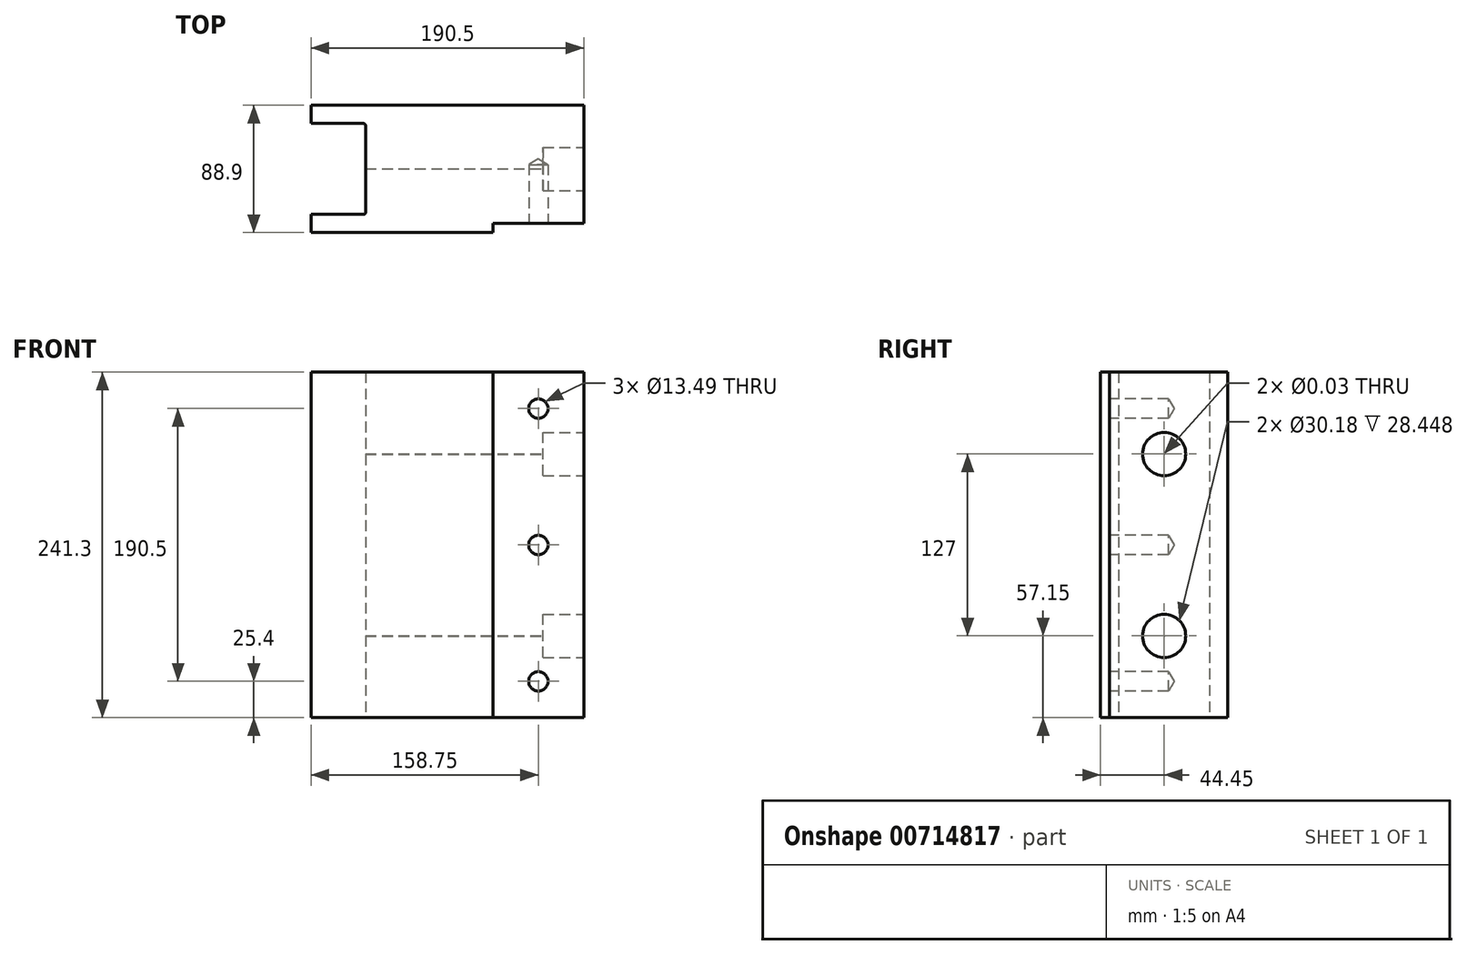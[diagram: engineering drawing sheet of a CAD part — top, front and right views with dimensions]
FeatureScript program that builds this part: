
annotation { "Feature Type Name" : "Feature", "Feature Type Description" : "" }
export const myFeature = defineFeature(function(context is Context, id is Id, definition is map)
    precondition{}
    {
        {
            var Q0;
            Q0=qCreatedBy(makeId("Top.planeOp"),FACE);
            var sketch = newSketch(context, id + "F0", { "sketchPlane" : qUnion([Q0])});
            skLineSegment(sketch, "E0.bottom", {"start": v(-95.25, 44.45) * mm, "end": v(95.25, 44.45) * mm});
            skLineSegment(sketch, "E0.top", {"start": v(-95.25, -44.45) * mm, "end": v(95.25, -44.45) * mm});
            skLineSegment(sketch, "E0.left", {"start": v(-95.25, 44.45) * mm, "end": v(-95.25, 31.75) * mm});
            skLineSegment(sketch, "E0.right", {"start": v(95.25, 44.45) * mm, "end": v(95.25, -44.45) * mm});
            skPoint(sketch, "E0.middle", {"position": v(0, 0) * mm});
            skLineSegment(sketch, "E1.bottom", {"start": v(-57.15, -31.75) * mm, "end": v(-133.35, -31.75) * mm});
            skLineSegment(sketch, "E1.top", {"start": v(-57.15, 31.75) * mm, "end": v(-133.35, 31.75) * mm});
            skLineSegment(sketch, "E1.left", {"start": v(-57.15, -31.75) * mm, "end": v(-57.15, 31.75) * mm});
            skPoint(sketch, "E1.middle", {"position": v(-95.25, 0) * mm});
            skLineSegment(sketch, "E2.trimOffspring", {"start": v(-95.25, 0) * mm, "end": v(-95.25, -44.45) * mm});
            skSolve(sketch);
        }
        {
            var Q0;
            Q0 = qSketchRegion(id + "F0", true);
            extrude(context, id + "F1", {"entities" : qUnion([Q0]), "endBound" : BoundingType.SYMMETRIC, "depth" : 241.3 * mm, "offsetDistance" : 25.4 * mm});
        }
        {
            var Q0;
            Q0=makeQuery(id+"F1.opExtrude","SWEPT_EDGE",EDGE,{"disambiguationData":[OSD([sQuery(id+"F0.wireOp",EDGE,"E1.top"),sQuery(id+"F0.wireOp",EDGE,"E1.left")])]});
            var Q1;
            Q1=makeQuery(id+"F1.opExtrude","SWEPT_EDGE",EDGE,{"disambiguationData":[OSD([sQuery(id+"F0.wireOp",EDGE,"E1.bottom"),sQuery(id+"F0.wireOp",EDGE,"E1.left")])]});
            fillet(context, id + "F2", {"entities" : qUnion([Q0, Q1]), "radius" : 1.52 * mm, "tangentPropagation" : true, "allowEdgeOverflow" : false});
        }
        {
            var Q0;
            Q0=makeQuery(id+"F1.opExtrude","SWEPT_FACE",FACE,{"disambiguationData":[OSD([sQuery(id+"F0.wireOp",EDGE,"E0.right")])]});
            var sketch = newSketch(context, id + "F3", { "sketchPlane" : qUnion([Q0])});
            skLineSegment(sketch, "E3", {"start": v(0, -145.44) * mm, "end": v(0, 141.68) * mm, "construction": true});
            skLineSegment(sketch, "E4.0", {"start": v(44.45, -120.65) * mm, "end": v(-44.45, -120.65) * mm, "construction": true});
            skLineSegment(sketch, "E5.0", {"start": v(44.45, -63.5) * mm, "end": v(-44.45, -63.5) * mm, "construction": true});
            skLineSegment(sketch, "E6.0", {"start": v(44.45, 63.5) * mm, "end": v(-44.45, 63.5) * mm, "construction": true});
            skPoint(sketch, "E7", {"position": v(0, 63.5) * mm});
            skPoint(sketch, "E8", {"position": v(0, -63.5) * mm});
            skSolve(sketch);
        }
        {
            var Q0;
            Q0=sQuery(id+"F3.wireOp",VERTEX,"E7");
            var Q1;
            Q1=sQuery(id+"F3.wireOp",VERTEX,"E8");
            var Q2;
            Q2=makeQuery(id+"F1.opExtrude","SWEPT_BODY",BODY,{"disambiguationData":[OSD([sQuery(id+"F0.wireOp",EDGE,"E0.bottom"),sQuery(id+"F0.wireOp",EDGE,"E0.top"),sQuery(id+"F0.wireOp",EDGE,"E0.left"),sQuery(id+"F0.wireOp",EDGE,"E0.right"),sQuery(id+"F0.wireOp",EDGE,"E1.bottom"),sQuery(id+"F0.wireOp",EDGE,"E1.top"),sQuery(id+"F0.wireOp",EDGE,"E1.left"),sQuery(id+"F0.wireOp",EDGE,"E2.trimOffspring")])]});
            hole(context, id + "F4", {"style" : HoleStyle.C_BORE, "endStyle" : HoleEndStyle.THROUGH, "standardTappedOrClearance" : lookupTablePath({ "standard" : "ANSI", "size" : "13/16 (0.81)", "type" : "Drilled" }), "standardBlindInLast" : lookupTablePath({ "standard" : "ANSI", "size" : "13/16", "type" : "Drilled" }), "holeDiameter" : 13 / 406.4 * mm, "cBoreDiameter" : 30.18 * mm, "cBoreDepth" : 28.45 * mm, "majorDiameter" : 6.35 * mm, "isTappedThrough" : true, "tappedDepth" : 34.3 * mm, "tapClearance" : 3, "locations" : qUnion([Q0, Q1]), "scope" : qUnion([Q2])});
        }
        {
            var Q0;
            Q0=makeQuery(id+"F1.opExtrude","SWEPT_FACE",FACE,{"disambiguationData":[OSD([sQuery(id+"F0.wireOp",EDGE,"E0.top")])]});
            var sketch = newSketch(context, id + "F5", { "sketchPlane" : qUnion([Q0])});
            skLineSegment(sketch, "E9.bottom", {"start": v(95.25, 120.65) * mm, "end": v(31.75, 120.65) * mm});
            skLineSegment(sketch, "E9.top", {"start": v(95.25, -120.65) * mm, "end": v(31.75, -120.65) * mm});
            skLineSegment(sketch, "E9.left", {"start": v(95.25, 120.65) * mm, "end": v(95.25, -120.65) * mm});
            skLineSegment(sketch, "E9.right", {"start": v(31.75, 120.65) * mm, "end": v(31.75, -120.65) * mm});
            skSolve(sketch);
        }
        {
            var Q0;
            Q0 = qSketchRegion(id + "F5", true);
            extrude(context, id + "F6", {"entities" : qUnion([Q0]), "operationType" : NewBodyOperationType.REMOVE, "oppositeDirection" : true, "depth" : 6.35 * mm, "offsetDistance" : 25.4 * mm});
        }
        {
            var Q0;
            Q0=makeQuery(id+"F6.boolean.opBoolean","COPY",FACE,{"derivedFrom":makeQuery(id+"F6.opExtrude","CAP_FACE",FACE,{"disambiguationData":[OSD([sQuery(id+"F5.wireOp",EDGE,"E9.bottom"),sQuery(id+"F5.wireOp",EDGE,"E9.top"),sQuery(id+"F5.wireOp",EDGE,"E9.left"),sQuery(id+"F5.wireOp",EDGE,"E9.right")])],"isStart":false})});
            var sketch = newSketch(context, id + "F7", { "sketchPlane" : qUnion([Q0])});
            skLineSegment(sketch, "E10.0", {"start": v(95.25, 120.65) * mm, "end": v(95.25, -120.65) * mm, "construction": true});
            skLineSegment(sketch, "E11", {"start": v(173.2, 0) * mm, "end": v(-136.03, 0) * mm, "construction": true});
            skLineSegment(sketch, "E12.0", {"start": v(63.5, 120.65) * mm, "end": v(63.5, -120.65) * mm, "construction": true});
            skLineSegment(sketch, "E13.0", {"start": v(173.2, 95.25) * mm, "end": v(-136.03, 95.25) * mm, "construction": true});
            skPoint(sketch, "E14", {"position": v(63.5, 95.25) * mm});
            skPoint(sketch, "E15", {"position": v(63.5, 0) * mm});
            skPoint(sketch, "E16.MirrorP", {"position": v(63.5, -95.25) * mm});
            skSolve(sketch);
        }
        {
            var Q0;
            Q0=sQuery(id+"F7.wireOp",VERTEX,"E14");
            var Q1;
            Q1=sQuery(id+"F7.wireOp",VERTEX,"E15");
            var Q2;
            Q2=sQuery(id+"F7.wireOp",VERTEX,"E16.MirrorP");
            var Q3;
            Q3=makeQuery(id+"F1.opExtrude","SWEPT_BODY",BODY,{"disambiguationData":[OSD([sQuery(id+"F0.wireOp",EDGE,"E0.bottom"),sQuery(id+"F0.wireOp",EDGE,"E0.top"),sQuery(id+"F0.wireOp",EDGE,"E0.left"),sQuery(id+"F0.wireOp",EDGE,"E0.right"),sQuery(id+"F0.wireOp",EDGE,"E1.bottom"),sQuery(id+"F0.wireOp",EDGE,"E1.top"),sQuery(id+"F0.wireOp",EDGE,"E1.left"),sQuery(id+"F0.wireOp",EDGE,"E2.trimOffspring")])]});
            hole(context, id + "F8", {"style" : HoleStyle.SIMPLE, "endStyle" : HoleEndStyle.BLIND, "standardTappedOrClearance" : lookupTablePath({ "standard" : "ANSI", "engagement" : "75%", "pitch" : "11 tpi", "size" : "5/8", "type" : "Tapped" }), "standardBlindInLast" : lookupTablePath({ "standard" : "ANSI", "engagement" : "75%", "pitch" : "11 tpi", "size" : "5/8", "type" : "Tapped" }), "holeDiameter" : 13.5 * mm, "majorDiameter" : 15.88 * mm, "showTappedDepth" : true, "holeDepth" : 41.22 * mm, "isTappedThrough" : true, "tappedDepth" : 34.3 * mm, "tapClearance" : 3, "locations" : qUnion([Q0, Q1, Q2]), "scope" : qUnion([Q3])});
        }
    });
